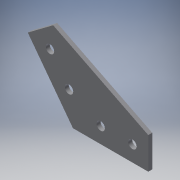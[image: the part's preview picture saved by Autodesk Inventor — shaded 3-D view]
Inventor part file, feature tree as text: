
AUTODESK INVENTOR PART (.ipt)
format: ipt  version: 2016 (Build 200138000, 138)  size: 110,080 bytes
history: native  units: in
note: dims shown in document units (in); Inventor stores cm internally (conversion verified against a paired STEP export)
features: extrude x1, sketch x1
ambient origin geometry x8: Origin, YZ Plane, XZ Plane, XY Plane, X Axis, Y Axis, Z Axis, Center Point
bodies: Solid1 (feature_tree)
feature tree (2):
  extrude  "Extrusion1"  Depth=0.125in
  sketch  "Sketch1"  dims[d0=2.875in d1=1.0in d2=1.0in d3=3.0in d4=0.8718in d5=0.2656in d6=1.0in d7=0.5in d8=0.5in d10=0.125in d11=0.0in d12=0.5in d13=1.0in d14=0.5in d15=1.5in]
